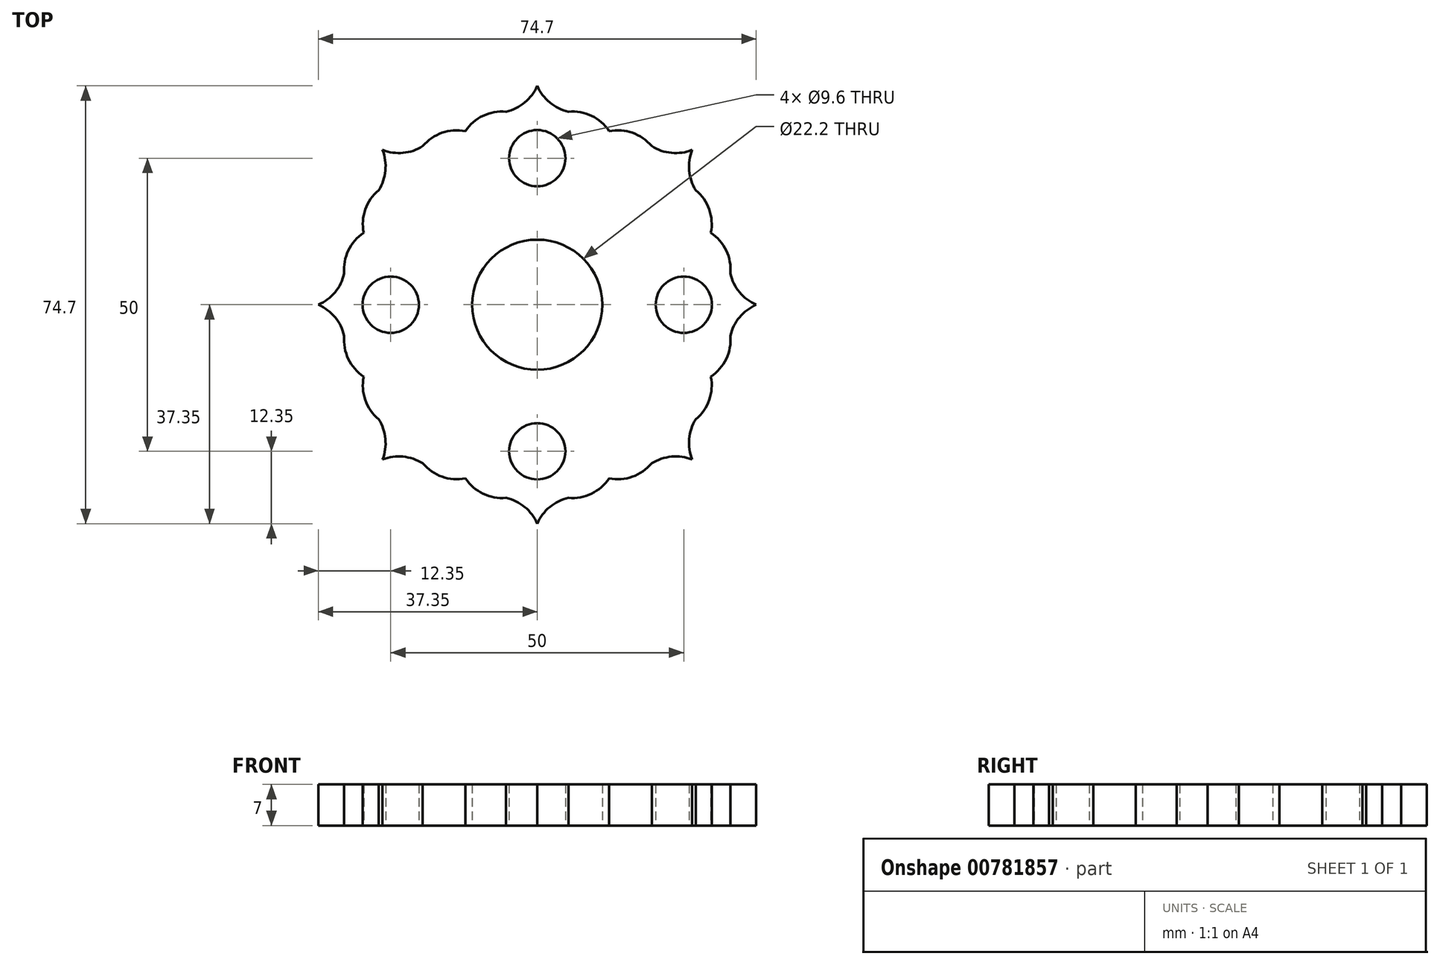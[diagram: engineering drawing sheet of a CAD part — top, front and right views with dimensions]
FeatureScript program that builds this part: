
annotation { "Feature Type Name" : "Feature", "Feature Type Description" : "" }
export const myFeature = defineFeature(function(context is Context, id is Id, definition is map)
    precondition{}
    {
        {
            var Q0;
            Q0=qCreatedBy(makeId("Top.planeOp"),FACE);
            var sketch = newSketch(context, id + "F0", { "sketchPlane" : qUnion([Q0])});
            skCircle(sketch, "E0", {"center": v(0, 0) * mm, "radius": 11.1 * mm});
            skCircle(sketch, "E1", {"center": v(25, 0) * mm, "radius": 4.8 * mm});
            skLineSegment(sketch, "E2", {"start": v(0, 0) * mm, "end": v(29.62, 12.27) * mm, "construction": true});
            skLineSegment(sketch, "E3.MirrorCS", {"start": v(0, 0) * mm, "end": v(29.62, -12.27) * mm, "construction": true});
            skArc(sketch, "E4", {"start": v(32.94, 5.32) * mm, "mid": v(32.24, 9.25) * mm, "end": v(29.62, 12.27) * mm});
            skArc(sketch, "E5", {"start": v(32.94, 5.32) * mm, "mid": v(34.51, 2.13) * mm, "end": v(37.35, 0) * mm});
            skArc(sketch, "E6.MirrorCS", {"start": v(32.94, -5.32) * mm, "mid": v(32.24, -9.25) * mm, "end": v(29.62, -12.27) * mm});
            skArc(sketch, "E7.MirrorCS", {"start": v(32.94, -5.32) * mm, "mid": v(34.51, -2.13) * mm, "end": v(37.35, 0) * mm});
            skArc(sketch, "E8.1.0", {"start": v(19.53, 27.05) * mm, "mid": v(22.9, 25.9) * mm, "end": v(26.41, 26.41) * mm});
            skArc(sketch, "E8.1.1", {"start": v(27.05, 19.53) * mm, "mid": v(25.9, 22.9) * mm, "end": v(26.41, 26.41) * mm});
            skArc(sketch, "E8.1.2", {"start": v(27.05, 19.53) * mm, "mid": v(29.34, 16.25) * mm, "end": v(29.62, 12.27) * mm});
            skArc(sketch, "E8.1.3", {"start": v(19.53, 27.05) * mm, "mid": v(16.25, 29.34) * mm, "end": v(12.27, 29.62) * mm});
            skArc(sketch, "E8.2.0", {"start": v(-5.32, 32.94) * mm, "mid": v(-2.13, 34.51) * mm, "end": v(0, 37.35) * mm});
            skArc(sketch, "E8.2.1", {"start": v(5.32, 32.94) * mm, "mid": v(2.13, 34.51) * mm, "end": v(0, 37.35) * mm});
            skArc(sketch, "E8.2.2", {"start": v(5.32, 32.94) * mm, "mid": v(9.25, 32.24) * mm, "end": v(12.27, 29.62) * mm});
            skArc(sketch, "E8.2.3", {"start": v(-5.32, 32.94) * mm, "mid": v(-9.25, 32.24) * mm, "end": v(-12.27, 29.62) * mm});
            skArc(sketch, "E8.3.0", {"start": v(-27.05, 19.53) * mm, "mid": v(-25.9, 22.9) * mm, "end": v(-26.41, 26.41) * mm});
            skArc(sketch, "E8.3.1", {"start": v(-19.53, 27.05) * mm, "mid": v(-22.9, 25.9) * mm, "end": v(-26.41, 26.41) * mm});
            skArc(sketch, "E8.3.2", {"start": v(-19.53, 27.05) * mm, "mid": v(-16.25, 29.34) * mm, "end": v(-12.27, 29.62) * mm});
            skArc(sketch, "E8.3.3", {"start": v(-27.05, 19.53) * mm, "mid": v(-29.34, 16.25) * mm, "end": v(-29.62, 12.27) * mm});
            skArc(sketch, "E8.4.0", {"start": v(-32.94, -5.32) * mm, "mid": v(-34.51, -2.13) * mm, "end": v(-37.35, 0) * mm});
            skArc(sketch, "E8.4.1", {"start": v(-32.94, 5.32) * mm, "mid": v(-34.51, 2.13) * mm, "end": v(-37.35, 0) * mm});
            skArc(sketch, "E8.4.2", {"start": v(-32.94, 5.32) * mm, "mid": v(-32.24, 9.25) * mm, "end": v(-29.62, 12.27) * mm});
            skArc(sketch, "E8.4.3", {"start": v(-32.94, -5.32) * mm, "mid": v(-32.24, -9.25) * mm, "end": v(-29.62, -12.27) * mm});
            skArc(sketch, "E8.5.0", {"start": v(-19.53, -27.05) * mm, "mid": v(-22.9, -25.9) * mm, "end": v(-26.41, -26.41) * mm});
            skArc(sketch, "E8.5.1", {"start": v(-27.05, -19.53) * mm, "mid": v(-25.9, -22.9) * mm, "end": v(-26.41, -26.41) * mm});
            skArc(sketch, "E8.5.2", {"start": v(-27.05, -19.53) * mm, "mid": v(-29.34, -16.25) * mm, "end": v(-29.62, -12.27) * mm});
            skArc(sketch, "E8.5.3", {"start": v(-19.53, -27.05) * mm, "mid": v(-16.25, -29.34) * mm, "end": v(-12.27, -29.62) * mm});
            skArc(sketch, "E8.6.0", {"start": v(5.32, -32.94) * mm, "mid": v(2.13, -34.51) * mm, "end": v(0, -37.35) * mm});
            skArc(sketch, "E8.6.1", {"start": v(-5.32, -32.94) * mm, "mid": v(-2.13, -34.51) * mm, "end": v(0, -37.35) * mm});
            skArc(sketch, "E8.6.2", {"start": v(-5.32, -32.94) * mm, "mid": v(-9.25, -32.24) * mm, "end": v(-12.27, -29.62) * mm});
            skArc(sketch, "E8.6.3", {"start": v(5.32, -32.94) * mm, "mid": v(9.25, -32.24) * mm, "end": v(12.27, -29.62) * mm});
            skArc(sketch, "E8.7.0", {"start": v(27.05, -19.53) * mm, "mid": v(25.9, -22.9) * mm, "end": v(26.41, -26.41) * mm});
            skArc(sketch, "E8.7.1", {"start": v(19.53, -27.05) * mm, "mid": v(22.9, -25.9) * mm, "end": v(26.41, -26.41) * mm});
            skArc(sketch, "E8.7.2", {"start": v(19.53, -27.05) * mm, "mid": v(16.25, -29.34) * mm, "end": v(12.27, -29.62) * mm});
            skArc(sketch, "E8.7.3", {"start": v(27.05, -19.53) * mm, "mid": v(29.34, -16.25) * mm, "end": v(29.62, -12.27) * mm});
            skCircle(sketch, "E9.1.0", {"center": v(0, 25) * mm, "radius": 4.8 * mm});
            skCircle(sketch, "E9.2.0", {"center": v(-25, 0) * mm, "radius": 4.8 * mm});
            skCircle(sketch, "E9.3.0", {"center": v(0, -25) * mm, "radius": 4.8 * mm});
            skSolve(sketch);
        }
        {
            var Q0;
            Q0=makeQuery(id+"F0.imprint","IMPRINT",FACE,{"disambiguationData":[TD([[makeQuery(id+"F0.imprint","IMPRINT",EDGE,{"derivedFrom":sQuery(id+"F0.wireOp",EDGE,"E0")}),-1.0]])]});
            extrude(context, id + "F1", {"entities" : qUnion([Q0]), "depth" : 7 * mm, "offsetDistance" : 25 * mm});
        }
    });
